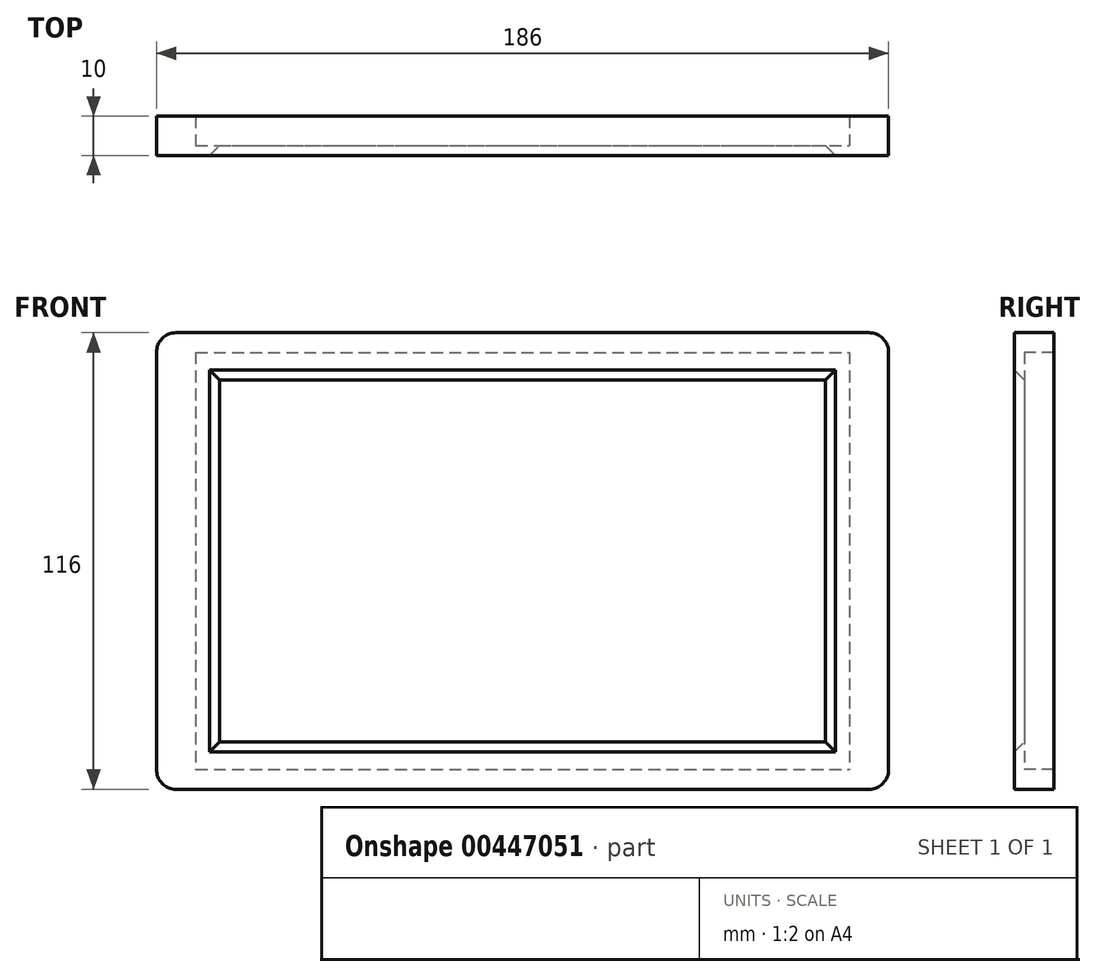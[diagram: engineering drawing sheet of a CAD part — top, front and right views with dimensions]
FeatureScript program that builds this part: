
annotation { "Feature Type Name" : "Feature", "Feature Type Description" : "" }
export const myFeature = defineFeature(function(context is Context, id is Id, definition is map)
    precondition{}
    {
        {
            var Q0;
            Q0=qCreatedBy(makeId("Front.planeOp"),FACE);
            var sketch = newSketch(context, id + "F0", { "sketchPlane" : qUnion([Q0])});
            skLineSegment(sketch, "E0.bottom", {"start": v(-77, 46) * mm, "end": v(77, 46) * mm});
            skLineSegment(sketch, "E0.top", {"start": v(-77, -46) * mm, "end": v(77, -46) * mm});
            skLineSegment(sketch, "E0.left", {"start": v(-77, 46) * mm, "end": v(-77, -46) * mm});
            skLineSegment(sketch, "E0.right", {"start": v(77, 46) * mm, "end": v(77, -46) * mm});
            skPoint(sketch, "E0.middle", {"position": v(0, 0) * mm});
            skLineSegment(sketch, "E1.bottom", {"start": v(-83, 53) * mm, "end": v(83, 53) * mm});
            skLineSegment(sketch, "E1.top", {"start": v(-83, -53) * mm, "end": v(83, -53) * mm});
            skLineSegment(sketch, "E1.left", {"start": v(-83, 53) * mm, "end": v(-83, -53) * mm});
            skLineSegment(sketch, "E1.right", {"start": v(83, 53) * mm, "end": v(83, -53) * mm});
            skLineSegment(sketch, "E2.bottom", {"start": v(-93, 58) * mm, "end": v(93, 58) * mm});
            skLineSegment(sketch, "E2.top", {"start": v(-93, -58) * mm, "end": v(93, -58) * mm});
            skLineSegment(sketch, "E2.left", {"start": v(-93, 58) * mm, "end": v(-93, -58) * mm});
            skLineSegment(sketch, "E2.right", {"start": v(93, 58) * mm, "end": v(93, -58) * mm});
            skLineSegment(sketch, "E3.bottom", {"start": v(-82, 51) * mm, "end": v(82, 51) * mm});
            skLineSegment(sketch, "E3.top", {"start": v(-82, -51) * mm, "end": v(82, -51) * mm});
            skLineSegment(sketch, "E3.left", {"start": v(-82, 51) * mm, "end": v(-82, -51) * mm});
            skLineSegment(sketch, "E3.right", {"start": v(82, 51) * mm, "end": v(82, -51) * mm});
            skSolve(sketch);
        }
        {
            var Q0;
            Q0=makeQuery(id+"F0.imprint","IMPRINT",FACE,{"disambiguationData":[TD([[makeQuery(id+"F0.imprint","IMPRINT",EDGE,{"derivedFrom":sQuery(id+"F0.wireOp",EDGE,"E1.bottom")}),1.0]])]});
            extrude(context, id + "F1", {"entities" : qUnion([Q0]), "oppositeDirection" : true, "depth" : 10 * mm});
        }
        {
            var Q0;
            Q0=makeQuery(id+"F0.imprint","IMPRINT",FACE,{"disambiguationData":[TD([[makeQuery(id+"F0.imprint","IMPRINT",EDGE,{"derivedFrom":sQuery(id+"F0.wireOp",EDGE,"E1.bottom")}),-1.0]])]});
            extrude(context, id + "F2", {"entities" : qUnion([Q0]), "operationType" : NewBodyOperationType.ADD, "oppositeDirection" : true, "depth" : 2.5 * mm});
        }
        {
            var Q0;
            Q0=makeQuery(id+"F0.imprint","IMPRINT",FACE,{"disambiguationData":[TD([[makeQuery(id+"F0.imprint","IMPRINT",EDGE,{"derivedFrom":sQuery(id+"F0.wireOp",EDGE,"E0.bottom")}),1.0]])]});
            extrude(context, id + "F3", {"entities" : qUnion([Q0]), "operationType" : NewBodyOperationType.ADD, "oppositeDirection" : true, "depth" : 2.5 * mm});
        }
        {
            var Q0;
            Q0=makeQuery(id+"F3.opExtrude","CAP_EDGE",EDGE,{"disambiguationData":[OSD([sQuery(id+"F0.wireOp",EDGE,"E0.bottom")])],"isStart":true});
            var Q1;
            Q1=makeQuery(id+"F3.opExtrude","CAP_EDGE",EDGE,{"disambiguationData":[OSD([sQuery(id+"F0.wireOp",EDGE,"E0.left")])],"isStart":true});
            var Q2;
            Q2=makeQuery(id+"F3.opExtrude","CAP_EDGE",EDGE,{"disambiguationData":[OSD([sQuery(id+"F0.wireOp",EDGE,"E0.top")])],"isStart":true});
            var Q3;
            Q3=makeQuery(id+"F3.opExtrude","CAP_EDGE",EDGE,{"disambiguationData":[OSD([sQuery(id+"F0.wireOp",EDGE,"E0.right")])],"isStart":true});
            chamfer(context, id + "F4", {"entities" : qUnion([Q0, Q1, Q2, Q3]), "width" : 2.5 * mm, "tangentPropagation" : true});
        }
        {
            var Q0;
            Q0=makeQuery(id+"F1.opExtrude","SWEPT_EDGE",EDGE,{"disambiguationData":[OSD([sQuery(id+"F0.wireOp",EDGE,"E2.bottom"),sQuery(id+"F0.wireOp",EDGE,"E2.left")])]});
            var Q1;
            Q1=makeQuery(id+"F1.opExtrude","SWEPT_EDGE",EDGE,{"disambiguationData":[OSD([sQuery(id+"F0.wireOp",EDGE,"E2.top"),sQuery(id+"F0.wireOp",EDGE,"E2.left")])]});
            var Q2;
            Q2=makeQuery(id+"F1.opExtrude","SWEPT_EDGE",EDGE,{"disambiguationData":[OSD([sQuery(id+"F0.wireOp",EDGE,"E2.top"),sQuery(id+"F0.wireOp",EDGE,"E2.right")])]});
            var Q3;
            Q3=makeQuery(id+"F1.opExtrude","SWEPT_EDGE",EDGE,{"disambiguationData":[OSD([sQuery(id+"F0.wireOp",EDGE,"E2.bottom"),sQuery(id+"F0.wireOp",EDGE,"E2.right")])]});
            fillet(context, id + "F5", {"entities" : qUnion([Q0, Q1, Q2, Q3]), "radius" : 5 * mm, "tangentPropagation" : true, "allowEdgeOverflow" : false});
        }
    });
